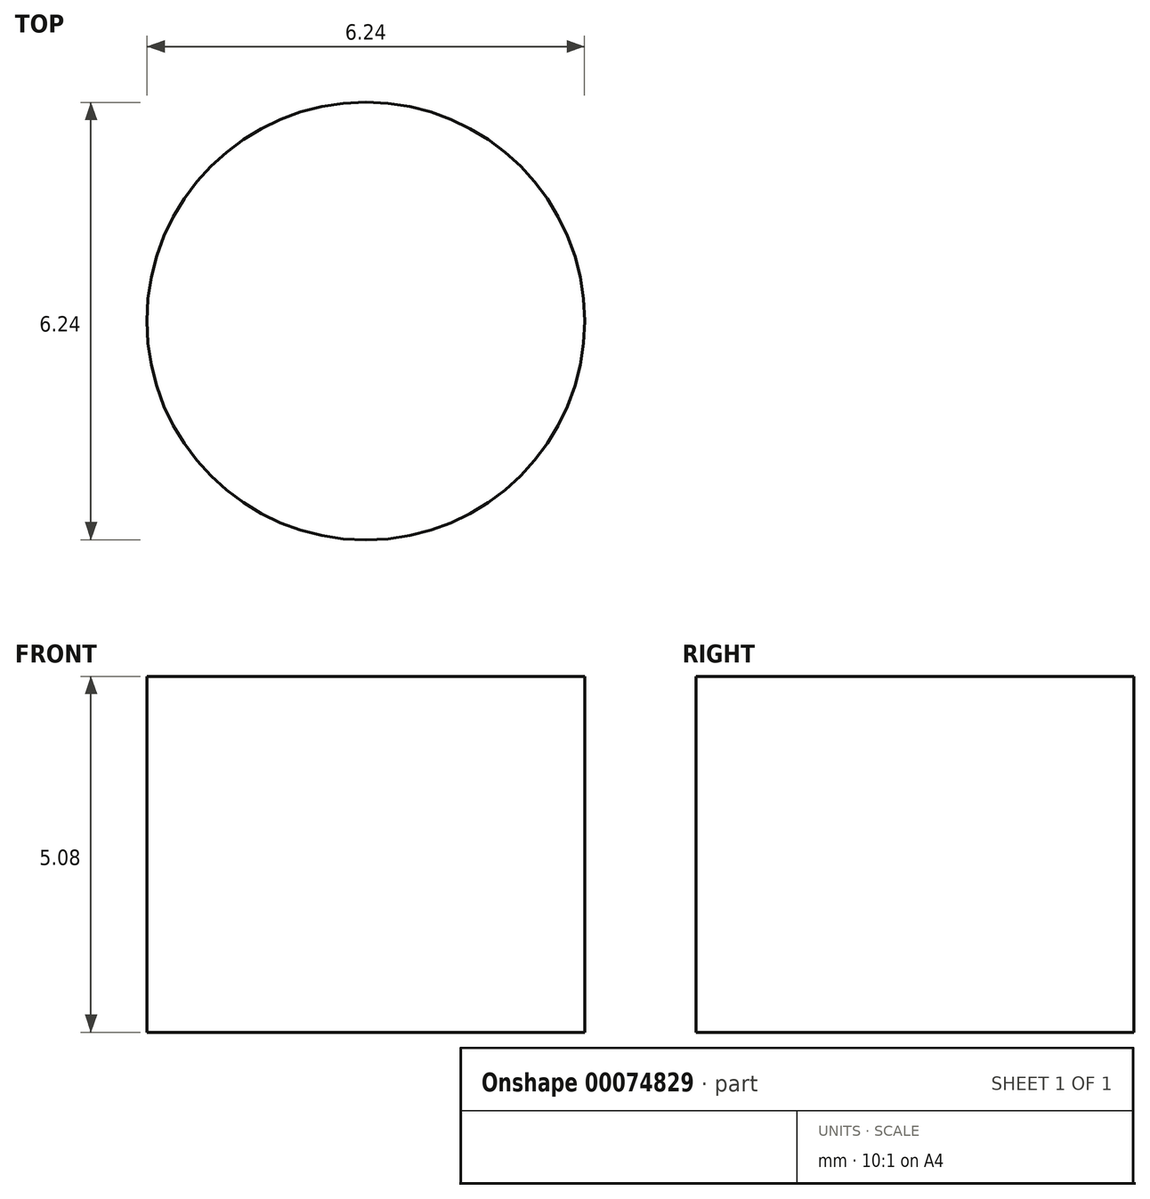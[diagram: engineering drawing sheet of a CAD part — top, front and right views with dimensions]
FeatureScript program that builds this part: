
annotation { "Feature Type Name" : "Feature", "Feature Type Description" : "" }
export const myFeature = defineFeature(function(context is Context, id is Id, definition is map)
    precondition{}
    {
        {
            var Q0;
            Q0=qCreatedBy(makeId("Right.planeOp"),FACE);
            var sketch = newSketch(context, id + "F0", { "sketchPlane" : qUnion([Q0])});
            skLineSegment(sketch, "E0.bottom", {"start": v(0, 0) * mm, "end": v(3.12, 0) * mm});
            skLineSegment(sketch, "E0.top", {"start": v(0, 5.08) * mm, "end": v(3.12, 5.08) * mm});
            skLineSegment(sketch, "E0.left", {"start": v(0, 0) * mm, "end": v(0, 5.08) * mm});
            skLineSegment(sketch, "E0.right", {"start": v(3.12, 0) * mm, "end": v(3.12, 5.08) * mm});
            skSolve(sketch);
        }
        {
            var Q0;
            Q0 = qSketchRegion(id + "F0", true);
            var Q1;
            Q1=sQuery(id+"F0.wireOp",EDGE,"E0.left");
            revolve(context, id + "F1", {"entities" : qUnion([Q0]), "axis" : qUnion([Q1]), "revolveType" : RevolveType.FULL});
        }
        {
            var Q0;
            Q0=qCreatedBy(makeId("Top.planeOp"),FACE);
            var sketch = newSketch(context, id + "F2", { "sketchPlane" : qUnion([Q0])});
            skCircle(sketch, "E1", {"center": v(0, 0) * mm, "radius": 3.12 * mm});
            skSolve(sketch);
        }
        {
            var Q0;
            Q0 = qSketchRegion(id + "F2", true);
            extrude(context, id + "F3", {"entities" : qUnion([Q0]), "depth" : 5.08 * mm});
        }
    });
